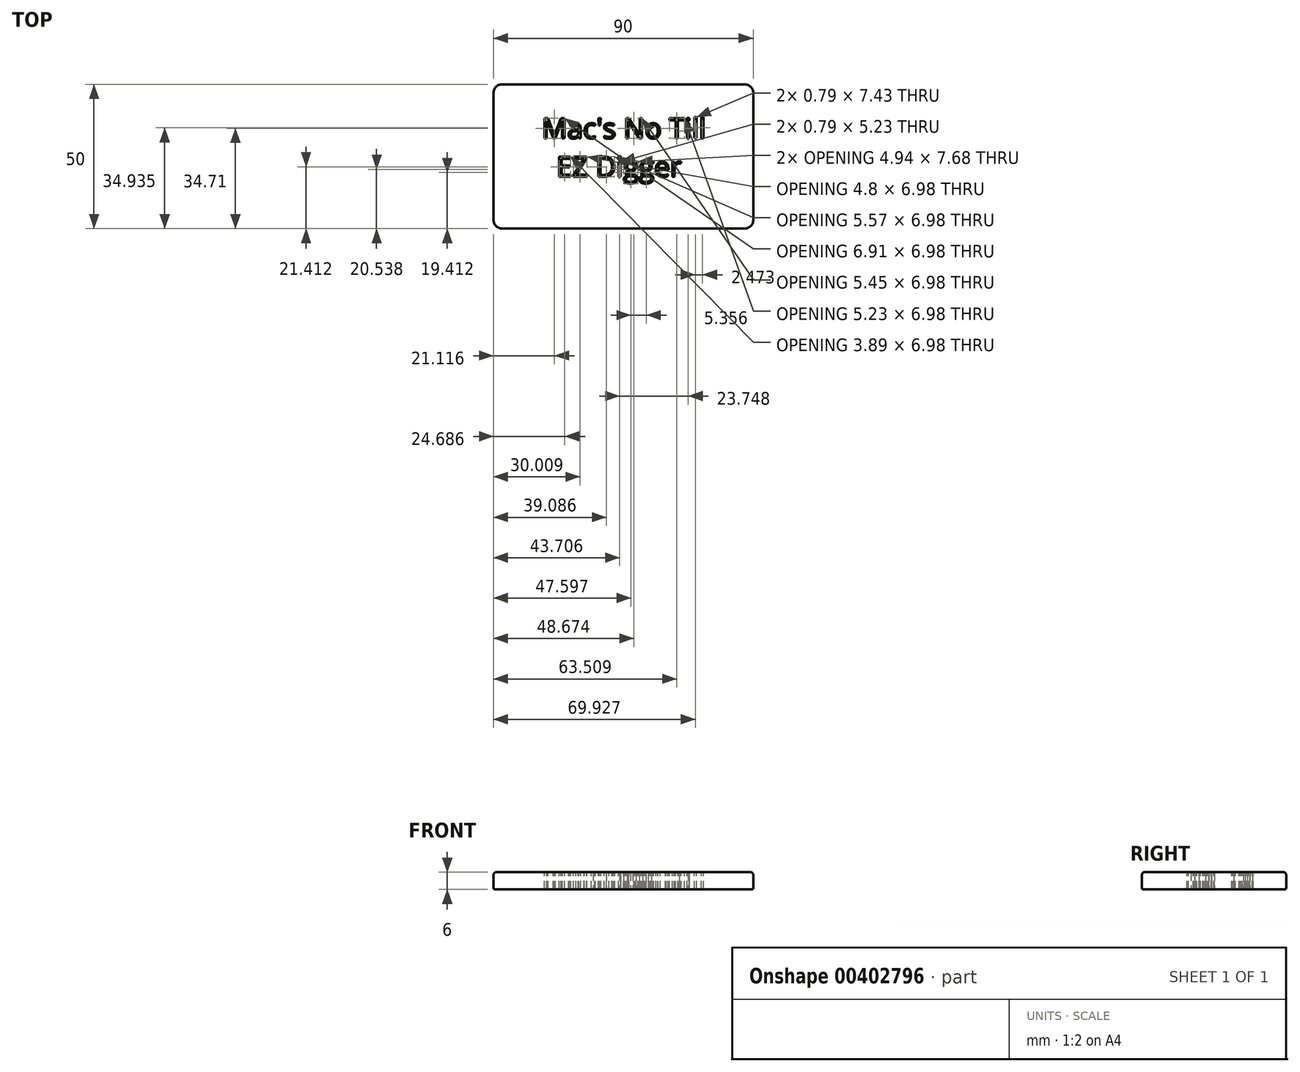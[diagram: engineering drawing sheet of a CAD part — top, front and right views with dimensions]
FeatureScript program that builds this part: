
annotation { "Feature Type Name" : "Feature", "Feature Type Description" : "" }
export const myFeature = defineFeature(function(context is Context, id is Id, definition is map)
    precondition{}
    {
        {
            var Q0;
            Q0=qCreatedBy(makeId("Top.planeOp"),FACE);
            var sketch = newSketch(context, id + "F0", { "sketchPlane" : qUnion([Q0])});
            skLineSegment(sketch, "E0.bottom", {"start": v(45, 25) * mm, "end": v(-45, 25) * mm});
            skLineSegment(sketch, "E0.top", {"start": v(45, -25) * mm, "end": v(-45, -25) * mm});
            skLineSegment(sketch, "E0.left", {"start": v(45, 25) * mm, "end": v(45, -25) * mm});
            skLineSegment(sketch, "E0.right", {"start": v(-45, 25) * mm, "end": v(-45, -25) * mm});
            skPoint(sketch, "E0.middle", {"position": v(0, 0) * mm});
            skSolve(sketch);
        }
        {
            var Q0;
            Q0 = qSketchRegion(id + "F0", true);
            extrude(context, id + "F1", {"entities" : qUnion([Q0]), "oppositeDirection" : true, "depth" : 6 * mm});
        }
        {
            var Q0;
            Q0=makeQuery(id+"F1.opExtrude","CAP_FACE",FACE,{"disambiguationData":[OSD([sQuery(id+"F0.wireOp",EDGE,"E0.bottom"),sQuery(id+"F0.wireOp",EDGE,"E0.top"),sQuery(id+"F0.wireOp",EDGE,"E0.left"),sQuery(id+"F0.wireOp",EDGE,"E0.right")])],"isStart":true});
            fillet(context, id + "F2", {"entities" : qUnion([Q0]), "radius" : 1 * mm, "tangentPropagation" : true, "allowEdgeOverflow" : false});
        }
        {
            var Q0;
            Q0=makeQuery(id+"F1.opExtrude","CAP_FACE",FACE,{"disambiguationData":[OSD([sQuery(id+"F0.wireOp",EDGE,"E0.bottom"),sQuery(id+"F0.wireOp",EDGE,"E0.top"),sQuery(id+"F0.wireOp",EDGE,"E0.left"),sQuery(id+"F0.wireOp",EDGE,"E0.right")])],"isStart":false});
            fillet(context, id + "F3", {"entities" : qUnion([Q0]), "radius" : .5 * mm, "tangentPropagation" : true, "allowEdgeOverflow" : false});
        }
        {
            var Q0;
            Q0=makeQuery(id+"F1.opExtrude","SWEPT_EDGE",EDGE,{"disambiguationData":[OSD([sQuery(id+"F0.wireOp",EDGE,"E0.top"),sQuery(id+"F0.wireOp",EDGE,"E0.right")])]});
            var Q1;
            Q1=makeQuery(id+"F1.opExtrude","SWEPT_EDGE",EDGE,{"disambiguationData":[OSD([sQuery(id+"F0.wireOp",EDGE,"E0.top"),sQuery(id+"F0.wireOp",EDGE,"E0.left")])]});
            var Q2;
            Q2=makeQuery(id+"F1.opExtrude","SWEPT_EDGE",EDGE,{"disambiguationData":[OSD([sQuery(id+"F0.wireOp",EDGE,"E0.bottom"),sQuery(id+"F0.wireOp",EDGE,"E0.right")])]});
            var Q3;
            Q3=makeQuery(id+"F1.opExtrude","SWEPT_EDGE",EDGE,{"disambiguationData":[OSD([sQuery(id+"F0.wireOp",EDGE,"E0.bottom"),sQuery(id+"F0.wireOp",EDGE,"E0.left")])]});
            fillet(context, id + "F4", {"entities" : qUnion([Q0, Q1, Q2, Q3]), "radius" : 3 * mm, "tangentPropagation" : true, "allowEdgeOverflow" : false});
        }
        {
            var Q0;
            Q0=makeQuery(id+"F1.opExtrude","CAP_FACE",FACE,{"disambiguationData":[OSD([sQuery(id+"F0.wireOp",EDGE,"E0.bottom"),sQuery(id+"F0.wireOp",EDGE,"E0.top"),sQuery(id+"F0.wireOp",EDGE,"E0.left"),sQuery(id+"F0.wireOp",EDGE,"E0.right")])],"isStart":true});
            var sketch = newSketch(context, id + "F5", { "sketchPlane" : qUnion([Q0])});
            skText(sketch, "E1", { "text": "Mac\'s No Till\n  EZ Digger", "fontName": "OpenSans-Regular.ttf"});
            const initialGuessF5  = {"E1": [-0.0283, 0.00622, 1, 0, 0.00704]};
            skSetInitialGuess(sketch, initialGuessF5);
            skSolve(sketch);
        }
        {
            var Q0;
            Q0 = qSketchRegion(id + "F5", true);
            extrude(context, id + "F6", {"entities" : qUnion([Q0]), "operationType" : NewBodyOperationType.REMOVE, "endBound" : BoundingType.THROUGH_ALL, "oppositeDirection" : true, "depth" : 2 * mm});
        }
    });
